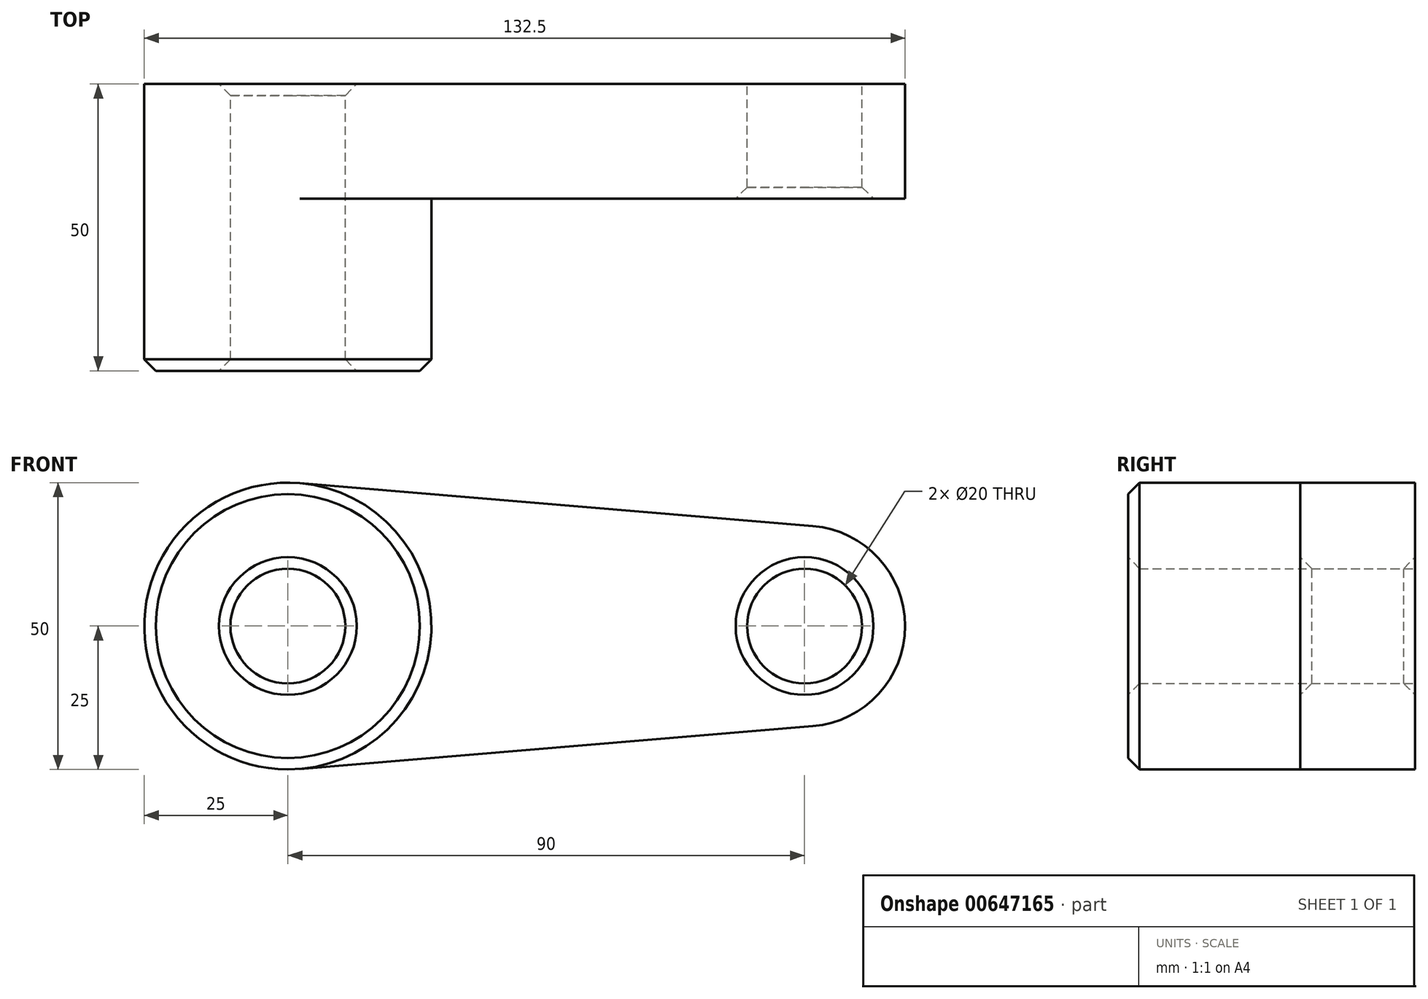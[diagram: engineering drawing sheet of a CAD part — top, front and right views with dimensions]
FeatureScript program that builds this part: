
annotation { "Feature Type Name" : "Feature", "Feature Type Description" : "" }
export const myFeature = defineFeature(function(context is Context, id is Id, definition is map)
    precondition{}
    {
        {
            var Q0;
            Q0=qCreatedBy(makeId("Front.planeOp"),FACE);
            var sketch = newSketch(context, id + "F0", { "sketchPlane" : qUnion([Q0])});
            skCircle(sketch, "E0", {"center": v(0, 0) * mm, "radius": 25 * mm});
            skCircle(sketch, "E1", {"center": v(90, 0) * mm, "radius": 17.5 * mm});
            skLineSegment(sketch, "E2", {"start": v(2.08, 24.91) * mm, "end": v(91.46, 17.44) * mm});
            skLineSegment(sketch, "E3", {"start": v(2.08, -24.91) * mm, "end": v(91.46, -17.44) * mm});
            skCircle(sketch, "E4", {"center": v(90, 0) * mm, "radius": 10 * mm});
            skCircle(sketch, "E5", {"center": v(0, 0) * mm, "radius": 10 * mm});
            skSolve(sketch);
        }
        {
            var Q0;
            Q0 = qSketchRegion(id + "F0", true);
            extrude(context, id + "F1", {"entities" : qUnion([Q0]), "depth" : 20 * mm, "offsetDistance" : 25 * mm});
        }
        {
            var Q0;
            Q0=makeQuery(id+"F0.imprint","IMPRINT",FACE,{"disambiguationData":[TD([[makeQuery(id+"F0.imprint","IMPRINT",EDGE,{"derivedFrom":sQuery(id+"F0.wireOp",EDGE,"E5")}),-1.0]])]});
            var Q1;
            Q1=sQuery(id+"F0.wireOp",EDGE,"E0");
            var Q2;
            Q2=sQuery(id+"F0.wireOp",EDGE,"E5");
            extrude(context, id + "F2", {"entities" : qUnion([Q0]), "operationType" : NewBodyOperationType.ADD, "surfaceEntities" : qUnion([Q1, Q2]), "depth" : 50 * mm, "offsetDistance" : 25 * mm});
        }
        {
            var Q0;
            {var subQ0=sQuery(id+"F0.wireOp",EDGE,"E5");Q0=makeQuery(id+"F2.boolean.opBoolean","MERGE",FACE,{"derivedFrom":[makeQuery(id+"F1.opExtrude","SWEPT_FACE",FACE,{"disambiguationData":[OSD([subQ0])]}),makeQuery(id+"F2.opExtrude","SWEPT_FACE",FACE,{"disambiguationData":[OSD([subQ0])]})]});}
            var Q1;
            Q1=makeQuery(id+"F2.opExtrude","CAP_EDGE",EDGE,{"disambiguationData":[OSD([sQuery(id+"F0.wireOp",EDGE,"E0")])],"isStart":false});
            var Q2;
            Q2=makeQuery(id+"F1.opExtrude","CAP_EDGE",EDGE,{"disambiguationData":[OSD([sQuery(id+"F0.wireOp",EDGE,"E4")])],"isStart":false});
            chamfer(context, id + "F3", {"entities" : qUnion([Q0, Q1, Q2]), "width" : 2 * mm, "tangentPropagation" : true});
        }
    });
